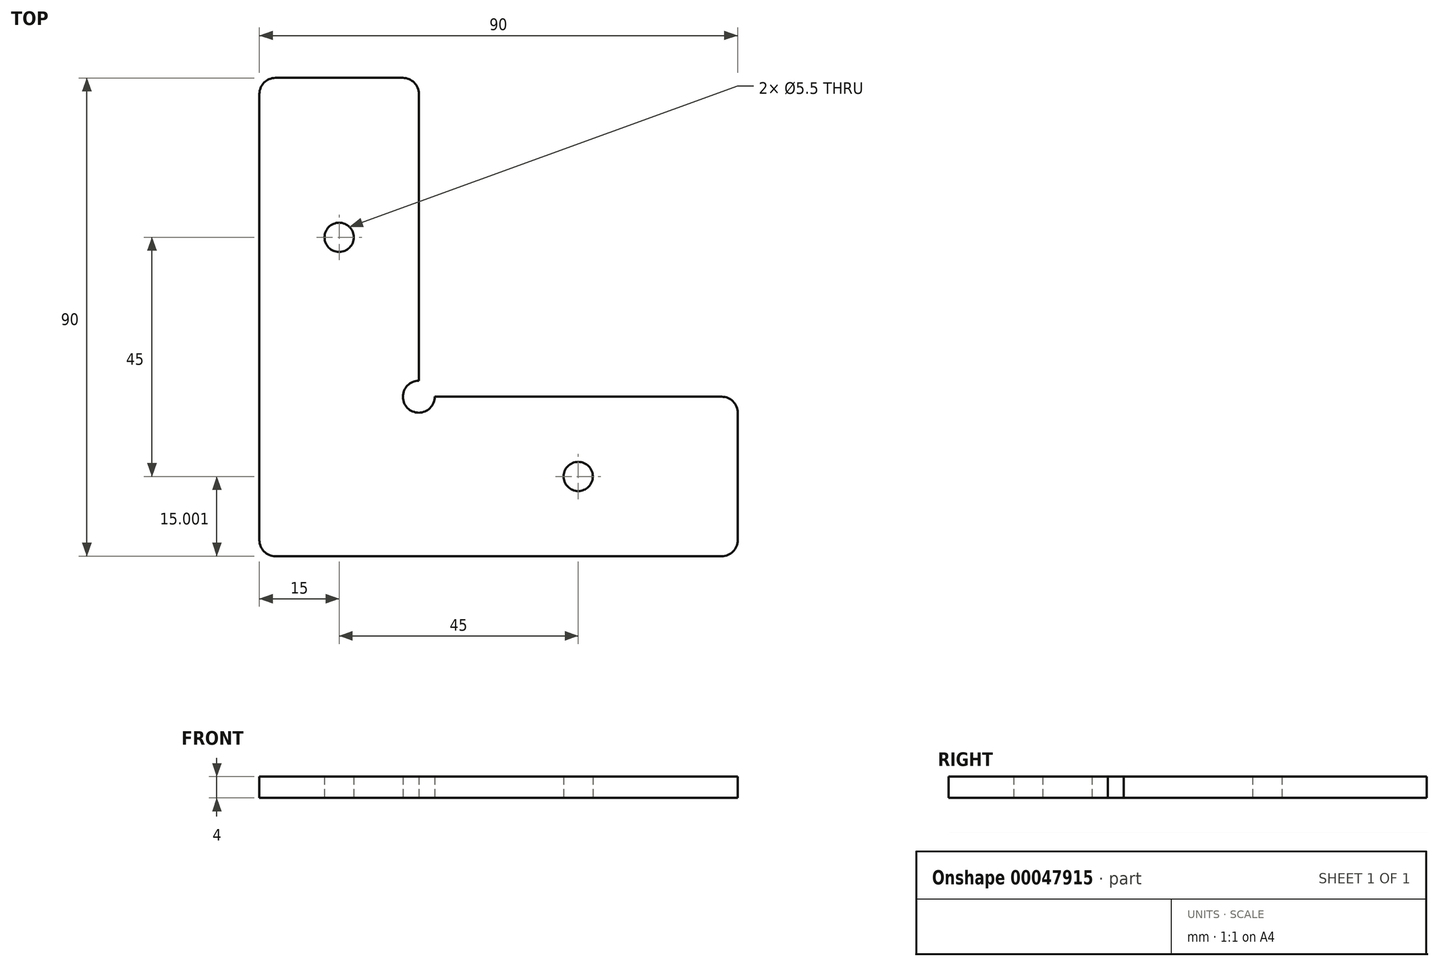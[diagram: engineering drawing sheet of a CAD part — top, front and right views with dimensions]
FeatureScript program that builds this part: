
annotation { "Feature Type Name" : "Feature", "Feature Type Description" : "" }
export const myFeature = defineFeature(function(context is Context, id is Id, definition is map)
    precondition{}
    {
        {
            var Q0;
            Q0=qCreatedBy(makeId("Top.planeOp"),FACE);
            var sketch = newSketch(context, id + "F0", { "sketchPlane" : qUnion([Q0])});
            skLineSegment(sketch, "E0.bottom", {"start": v(-27, 43.85) * mm, "end": v(-3, 43.85) * mm});
            skLineSegment(sketch, "E0.top", {"start": v(-27, -46.15) * mm, "end": v(0, -46.15) * mm});
            skLineSegment(sketch, "E0.left", {"start": v(-30, 40.85) * mm, "end": v(-30, -43.15) * mm});
            skLineSegment(sketch, "E0.right", {"start": v(0, 40.85) * mm, "end": v(0, -13.15) * mm});
            skLineSegment(sketch, "E1", {"start": v(3, -16.15) * mm, "end": v(57, -16.15) * mm});
            skLineSegment(sketch, "E2", {"start": v(60, -19.15) * mm, "end": v(60, -43.15) * mm});
            skLineSegment(sketch, "E3", {"start": v(57, -46.15) * mm, "end": v(0, -46.15) * mm});
            skCircle(sketch, "E4", {"center": v(-15, 13.85) * mm, "radius": 2.75 * mm});
            skPoint(sketch, "E4.centerSnap0", {"position": v(-15, 43.85) * mm});
            skCircle(sketch, "E5", {"center": v(30, -31.15) * mm, "radius": 2.75 * mm});
            skPoint(sketch, "E5.centerSnap0", {"position": v(60, -31.15) * mm});
            skPoint(sketch, "E6.visualSharp", {"position": v(-30, 43.85) * mm});
            skArc(sketch, "E6.filletArc", {"start": v(-27, 43.85) * mm, "mid": v(-29.12, 42.97) * mm, "end": v(-30, 40.85) * mm});
            skPoint(sketch, "E7.visualSharp", {"position": v(0, 43.85) * mm});
            skArc(sketch, "E7.filletArc", {"start": v(0, 40.85) * mm, "mid": v(-0.88, 42.97) * mm, "end": v(-3, 43.85) * mm});
            skPoint(sketch, "E8.visualSharp", {"position": v(60, -16.15) * mm});
            skArc(sketch, "E8.filletArc", {"start": v(60, -19.15) * mm, "mid": v(59.12, -17.03) * mm, "end": v(57, -16.15) * mm});
            skPoint(sketch, "E9.visualSharp", {"position": v(0, -16.15) * mm});
            skPoint(sketch, "E10.visualSharp", {"position": v(60, -46.15) * mm});
            skArc(sketch, "E10.filletArc", {"start": v(57, -46.15) * mm, "mid": v(59.12, -45.27) * mm, "end": v(60, -43.15) * mm});
            skPoint(sketch, "E11.visualSharp", {"position": v(-30, -46.15) * mm});
            skArc(sketch, "E11.filletArc", {"start": v(-30, -43.15) * mm, "mid": v(-29.12, -45.27) * mm, "end": v(-27, -46.15) * mm});
            skArc(sketch, "E12", {"start": v(0, -13.15) * mm, "mid": v(-2.12, -18.27) * mm, "end": v(3, -16.15) * mm});
            skSolve(sketch);
        }
        {
            var Q0;
            Q0=makeQuery(id+"F0.imprint","IMPRINT",FACE,{"disambiguationData":[TD([[makeQuery(id+"F0.imprint","IMPRINT",EDGE,{"derivedFrom":sQuery(id+"F0.wireOp",EDGE,"E0.bottom")}),-1.0]])]});
            extrude(context, id + "F1", {"entities" : qUnion([Q0]), "depth" : 4 * mm});
        }
    });
